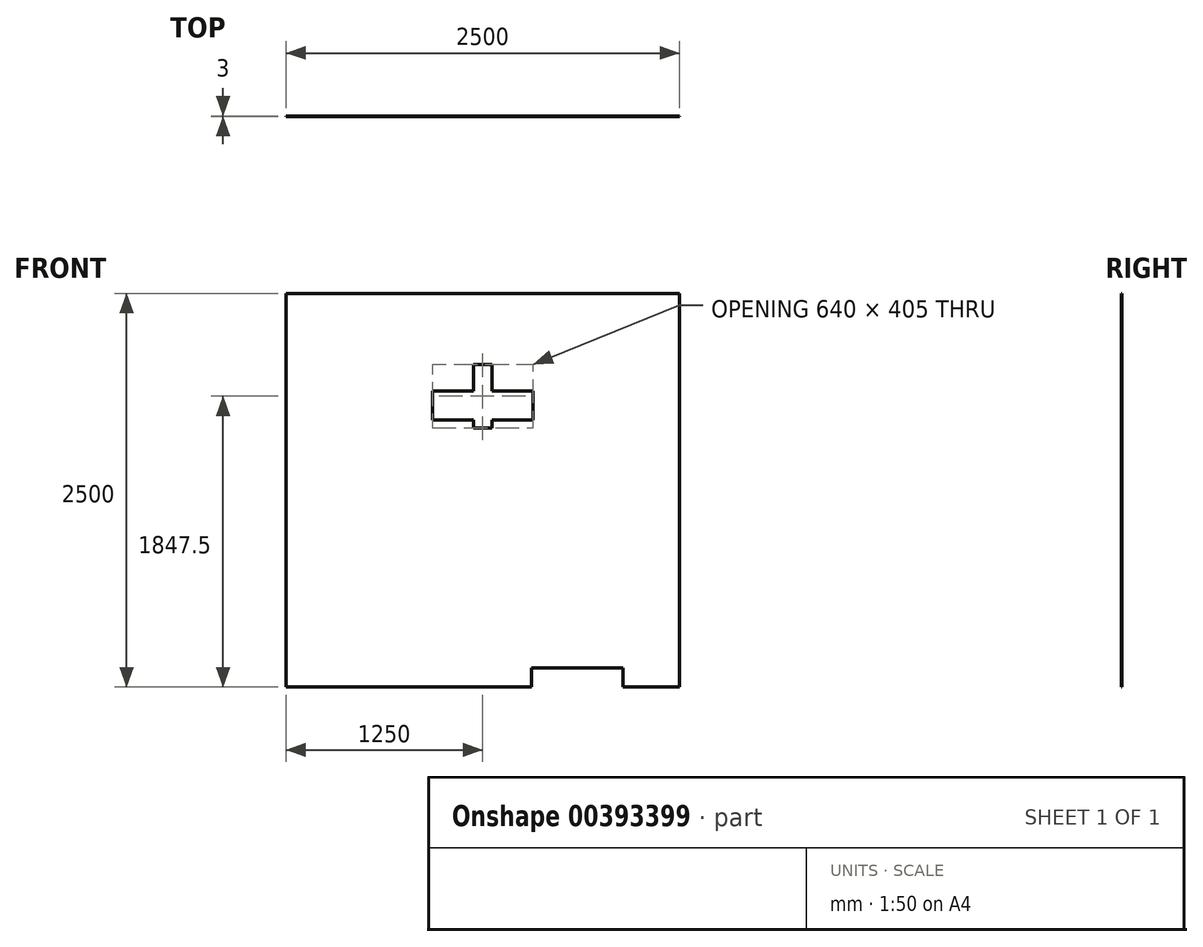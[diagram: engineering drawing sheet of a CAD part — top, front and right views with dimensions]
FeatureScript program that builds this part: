
annotation { "Feature Type Name" : "Feature", "Feature Type Description" : "" }
export const myFeature = defineFeature(function(context is Context, id is Id, definition is map)
    precondition{}
    {
        {
            var Q0;
            Q0=qCreatedBy(makeId("Front.planeOp"),FACE);
            var sketch = newSketch(context, id + "F0", { "sketchPlane" : qUnion([Q0])});
            skLineSegment(sketch, "E0.bottom", {"start": v(1250, 1250) * mm, "end": v(-1250, 1250) * mm});
            skLineSegment(sketch, "E0.top", {"start": v(1250, -1250) * mm, "end": v(890, -1250) * mm});
            skLineSegment(sketch, "E0.left", {"start": v(1250, 1250) * mm, "end": v(1250, -1250) * mm});
            skLineSegment(sketch, "E0.right", {"start": v(-1250, 1250) * mm, "end": v(-1250, -1250) * mm});
            skPoint(sketch, "E0.middle", {"position": v(0, 0) * mm});
            skLineSegment(sketch, "E1", {"start": v(-320, 630) * mm, "end": v(-60, 630) * mm});
            skLineSegment(sketch, "E2", {"start": v(-60, 630) * mm, "end": v(-60, 800) * mm});
            skLineSegment(sketch, "E3", {"start": v(-60, 800) * mm, "end": v(60, 800) * mm});
            skLineSegment(sketch, "E4", {"start": v(60, 800) * mm, "end": v(60, 630) * mm});
            skLineSegment(sketch, "E5", {"start": v(60, 630) * mm, "end": v(320, 630) * mm});
            skLineSegment(sketch, "E6", {"start": v(320, 630) * mm, "end": v(320, 445) * mm});
            skLineSegment(sketch, "E7", {"start": v(320, 445) * mm, "end": v(60, 445) * mm});
            skLineSegment(sketch, "E8", {"start": v(60, 445) * mm, "end": v(60, 395) * mm});
            skLineSegment(sketch, "E9", {"start": v(60, 395) * mm, "end": v(-60, 395) * mm});
            skLineSegment(sketch, "E10", {"start": v(-60, 395) * mm, "end": v(-60, 445) * mm});
            skLineSegment(sketch, "E11", {"start": v(-60, 445) * mm, "end": v(-320, 445) * mm});
            skLineSegment(sketch, "E12", {"start": v(-320, 445) * mm, "end": v(-320, 630) * mm});
            skLineSegment(sketch, "E13", {"start": v(0, 1250) * mm, "end": v(0, -1250) * mm, "construction": true});
            skPoint(sketch, "E14", {"position": v(0, 800) * mm});
            skLineSegment(sketch, "E15.top", {"start": v(890, -1130) * mm, "end": v(310, -1130) * mm});
            skLineSegment(sketch, "E15.left", {"start": v(890, -1250) * mm, "end": v(890, -1130) * mm});
            skLineSegment(sketch, "E15.right", {"start": v(310, -1250) * mm, "end": v(310, -1130) * mm});
            skLineSegment(sketch, "E16.trimOffspring", {"start": v(310, -1250) * mm, "end": v(-1250, -1250) * mm});
            skSolve(sketch);
        }
        {
            var Q0;
            Q0 = qSketchRegion(id + "F0", true);
            extrude(context, id + "F1", {"entities" : qUnion([Q0]), "depth" : 3 * mm});
        }
    });
